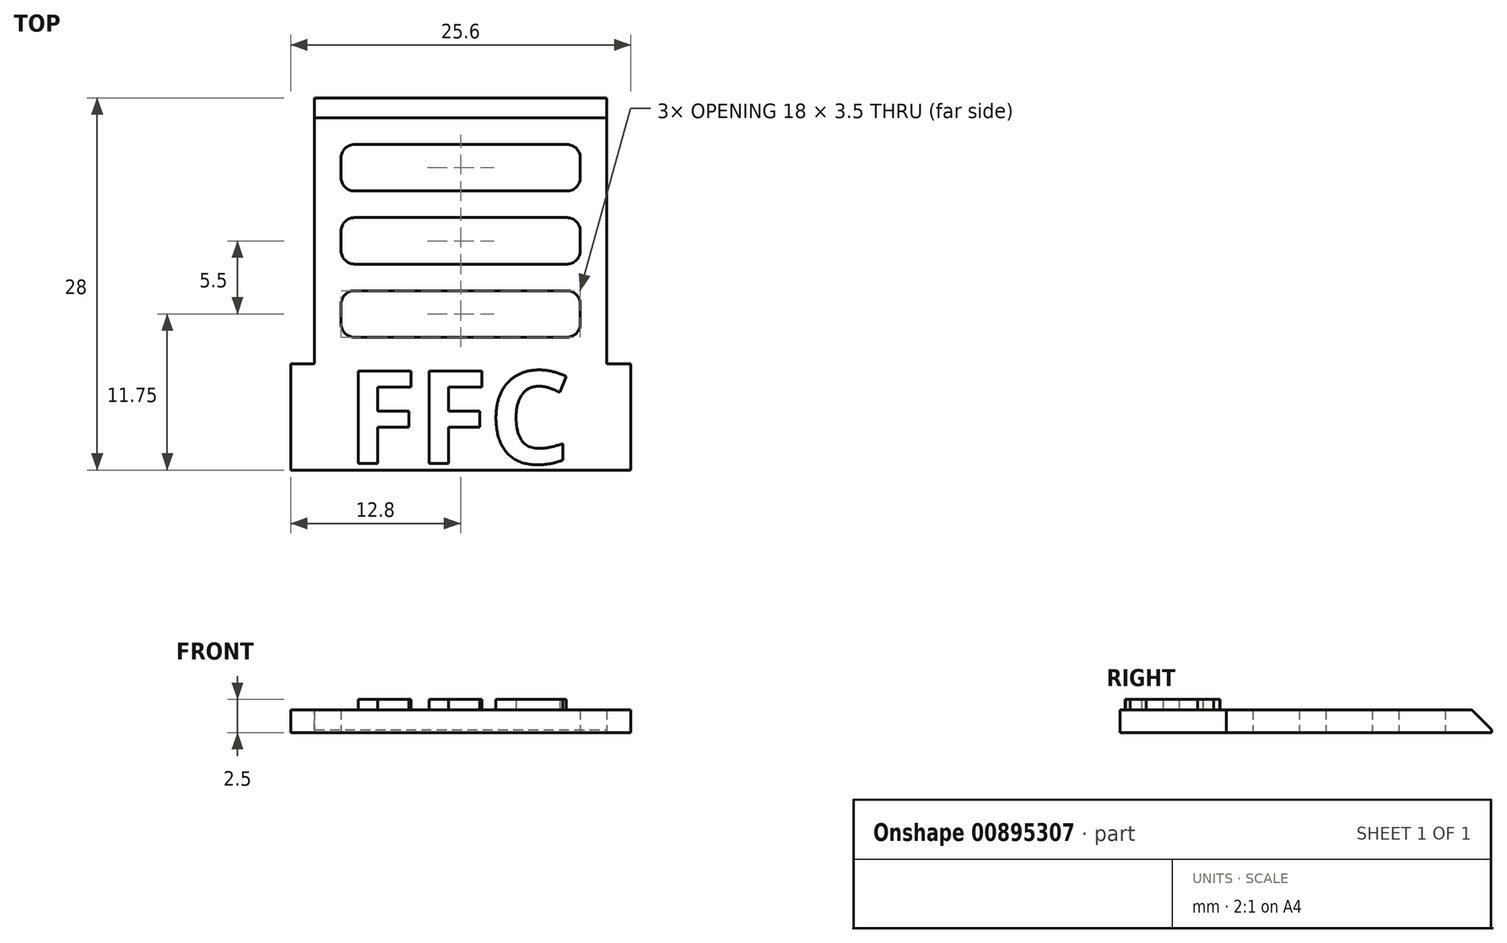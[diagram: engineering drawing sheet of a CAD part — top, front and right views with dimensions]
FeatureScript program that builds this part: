
annotation { "Feature Type Name" : "Feature", "Feature Type Description" : "" }
export const myFeature = defineFeature(function(context is Context, id is Id, definition is map)
    precondition{}
    {
        {
            var Q0;
            Q0=qCreatedBy(makeId("Top.planeOp"),FACE);
            var sketch = newSketch(context, id + "F0", { "sketchPlane" : qUnion([Q0])});
            skLineSegment(sketch, "E0.bottom", {"start": v(-11, 20) * mm, "end": v(11, 20) * mm});
            skLineSegment(sketch, "E0.top", {"start": v(-11, 0) * mm, "end": v(11, 0) * mm});
            skLineSegment(sketch, "E0.left", {"start": v(-11, 20) * mm, "end": v(-11, 0) * mm});
            skLineSegment(sketch, "E0.right", {"start": v(11, 20) * mm, "end": v(11, 0) * mm});
            skPoint(sketch, "E1", {"position": v(0, 0) * mm});
            skLineSegment(sketch, "E2.bottom", {"start": v(-12.8, 0) * mm, "end": v(12.8, 0) * mm});
            skLineSegment(sketch, "E2.top", {"start": v(-12.8, -8) * mm, "end": v(12.8, -8) * mm});
            skLineSegment(sketch, "E2.left", {"start": v(-12.8, 0) * mm, "end": v(-12.8, -8) * mm});
            skLineSegment(sketch, "E2.right", {"start": v(12.8, 0) * mm, "end": v(12.8, -8) * mm});
            skText(sketch, "E3", { "text": "FFC", "fontName": "OpenSans-Bold.ttf"});
            skLineSegment(sketch, "E4.bottom", {"start": v(-9, 16.5) * mm, "end": v(9, 16.5) * mm});
            skLineSegment(sketch, "E4.top", {"start": v(-9, 13) * mm, "end": v(9, 13) * mm});
            skLineSegment(sketch, "E4.left", {"start": v(-9, 16.5) * mm, "end": v(-9, 13) * mm});
            skLineSegment(sketch, "E4.right", {"start": v(9, 16.5) * mm, "end": v(9, 13) * mm});
            skLineSegment(sketch, "E5.bottom", {"start": v(-9, 11) * mm, "end": v(9, 11) * mm});
            skLineSegment(sketch, "E5.top", {"start": v(-9, 7.5) * mm, "end": v(9, 7.5) * mm});
            skLineSegment(sketch, "E5.left", {"start": v(-9, 11) * mm, "end": v(-9, 7.5) * mm});
            skLineSegment(sketch, "E5.right", {"start": v(9, 11) * mm, "end": v(9, 7.5) * mm});
            skLineSegment(sketch, "E6.bottom", {"start": v(-9, 5.5) * mm, "end": v(9, 5.5) * mm});
            skLineSegment(sketch, "E6.top", {"start": v(-9, 2) * mm, "end": v(9, 2) * mm});
            skLineSegment(sketch, "E6.left", {"start": v(-9, 5.5) * mm, "end": v(-9, 2) * mm});
            skLineSegment(sketch, "E6.right", {"start": v(9, 5.5) * mm, "end": v(9, 2) * mm});
            skLineSegment(sketch, "E7", {"start": v(-9, 5.5) * mm, "end": v(-9, 7.5) * mm, "construction": true});
            skLineSegment(sketch, "E8", {"start": v(-9, 11) * mm, "end": v(-9, 13) * mm, "construction": true});
            const initialGuessF0  = {"E3": [-0.00858, -0.0075, 1, 0, 0.007]};
            skSetInitialGuess(sketch, initialGuessF0);
            skSolve(sketch);
        }
        {
            var Q0;
            Q0=makeQuery(id+"F0.imprint","IMPRINT",FACE,{"disambiguationData":[TD([[makeQuery(id+"F0.imprint","IMPRINT",EDGE,{"derivedFrom":sQuery(id+"F0.wireOp",EDGE,"E2.top")}),1.0]])]});
            var Q1;
            Q1=makeQuery(id+"F0.imprint","IMPRINT",FACE,{"disambiguationData":[TD([[makeQuery(id+"F0.imprint","IMPRINT",EDGE,{"derivedFrom":sQuery(id+"F0.wireOp",EDGE,"E0.bottom")}),-1.0]])]});
            var Q2;
            Q2=makeQuery(id+"F0.imprint","IMPRINT",FACE,{"disambiguationData":[TD([[makeQuery(id+"F0.imprint","IMPRINT",EDGE,{"derivedFrom":sQuery(id+"F0.wireOp",EDGE,"E3.sketch_text.stroke-0")}),-1.0]])]});
            var Q3;
            Q3=makeQuery(id+"F0.imprint","IMPRINT",FACE,{"disambiguationData":[TD([[makeQuery(id+"F0.imprint","IMPRINT",EDGE,{"derivedFrom":sQuery(id+"F0.wireOp",EDGE,"E3.sketch_text.stroke-10")}),-1.0]])]});
            var Q4;
            Q4=makeQuery(id+"F0.imprint","IMPRINT",FACE,{"disambiguationData":[TD([[makeQuery(id+"F0.imprint","IMPRINT",EDGE,{"derivedFrom":sQuery(id+"F0.wireOp",EDGE,"E3.sketch_text.stroke-20")}),-1.0]])]});
            extrude(context, id + "F1", {"entities" : qUnion([Q0, Q1, Q2, Q3, Q4]), "depth" : 1.72 * mm, "offsetDistance" : 25 * mm});
        }
        {
            var Q0;
            Q0=makeQuery(id+"F0.imprint","IMPRINT",FACE,{"disambiguationData":[TD([[makeQuery(id+"F0.imprint","IMPRINT",EDGE,{"derivedFrom":sQuery(id+"F0.wireOp",EDGE,"E3.sketch_text.stroke-0")}),-1.0]])]});
            var Q1;
            Q1=makeQuery(id+"F0.imprint","IMPRINT",FACE,{"disambiguationData":[TD([[makeQuery(id+"F0.imprint","IMPRINT",EDGE,{"derivedFrom":sQuery(id+"F0.wireOp",EDGE,"E3.sketch_text.stroke-10")}),-1.0]])]});
            var Q2;
            Q2=makeQuery(id+"F0.imprint","IMPRINT",FACE,{"disambiguationData":[TD([[makeQuery(id+"F0.imprint","IMPRINT",EDGE,{"derivedFrom":sQuery(id+"F0.wireOp",EDGE,"E3.sketch_text.stroke-20")}),-1.0]])]});
            extrude(context, id + "F2", {"entities" : qUnion([Q0, Q1, Q2]), "operationType" : NewBodyOperationType.ADD, "depth" : 2.5 * mm, "offsetDistance" : 25 * mm});
        }
        {
            var Q0;
            Q0=makeQuery(id+"F1.opExtrude","CAP_EDGE",EDGE,{"disambiguationData":[OSD([sQuery(id+"F0.wireOp",EDGE,"E0.bottom")])],"isStart":false});
            chamfer(context, id + "F3", {"entities" : qUnion([Q0]), "width" : 1.5 * mm, "tangentPropagation" : true});
        }
        {
            var Q0;
            Q0=makeQuery(id+"F1.opExtrude","SWEPT_EDGE",EDGE,{"disambiguationData":[OSD([sQuery(id+"F0.wireOp",EDGE,"E4.bottom"),sQuery(id+"F0.wireOp",EDGE,"E4.left")])]});
            var Q1;
            Q1=makeQuery(id+"F1.opExtrude","SWEPT_EDGE",EDGE,{"disambiguationData":[OSD([sQuery(id+"F0.wireOp",EDGE,"E4.bottom"),sQuery(id+"F0.wireOp",EDGE,"E4.right")])]});
            var Q2;
            Q2=makeQuery(id+"F1.opExtrude","SWEPT_EDGE",EDGE,{"disambiguationData":[OSD([sQuery(id+"F0.wireOp",EDGE,"E5.bottom"),sQuery(id+"F0.wireOp",EDGE,"E5.right")])]});
            var Q3;
            Q3=makeQuery(id+"F1.opExtrude","SWEPT_EDGE",EDGE,{"disambiguationData":[OSD([sQuery(id+"F0.wireOp",EDGE,"E6.bottom"),sQuery(id+"F0.wireOp",EDGE,"E6.right")])]});
            var Q4;
            Q4=makeQuery(id+"F1.opExtrude","SWEPT_EDGE",EDGE,{"disambiguationData":[OSD([sQuery(id+"F0.wireOp",EDGE,"E4.top"),sQuery(id+"F0.wireOp",EDGE,"E4.right")])]});
            var Q5;
            Q5=makeQuery(id+"F1.opExtrude","SWEPT_EDGE",EDGE,{"disambiguationData":[OSD([sQuery(id+"F0.wireOp",EDGE,"E5.top"),sQuery(id+"F0.wireOp",EDGE,"E5.right")])]});
            var Q6;
            Q6=makeQuery(id+"F1.opExtrude","SWEPT_EDGE",EDGE,{"disambiguationData":[OSD([sQuery(id+"F0.wireOp",EDGE,"E6.top"),sQuery(id+"F0.wireOp",EDGE,"E6.right")])]});
            var Q7;
            Q7=makeQuery(id+"F1.opExtrude","SWEPT_EDGE",EDGE,{"disambiguationData":[OSD([sQuery(id+"F0.wireOp",EDGE,"E4.top"),sQuery(id+"F0.wireOp",EDGE,"E4.left")])]});
            var Q8;
            Q8=makeQuery(id+"F1.opExtrude","SWEPT_EDGE",EDGE,{"disambiguationData":[OSD([sQuery(id+"F0.wireOp",EDGE,"E5.top"),sQuery(id+"F0.wireOp",EDGE,"E5.left")])]});
            var Q9;
            Q9=makeQuery(id+"F1.opExtrude","SWEPT_EDGE",EDGE,{"disambiguationData":[OSD([sQuery(id+"F0.wireOp",EDGE,"E6.top"),sQuery(id+"F0.wireOp",EDGE,"E6.left")])]});
            var Q10;
            Q10=makeQuery(id+"F1.opExtrude","SWEPT_EDGE",EDGE,{"disambiguationData":[OSD([sQuery(id+"F0.wireOp",EDGE,"E6.bottom"),sQuery(id+"F0.wireOp",EDGE,"E6.left")])]});
            var Q11;
            Q11=makeQuery(id+"F1.opExtrude","SWEPT_EDGE",EDGE,{"disambiguationData":[OSD([sQuery(id+"F0.wireOp",EDGE,"E5.bottom"),sQuery(id+"F0.wireOp",EDGE,"E5.left")])]});
            fillet(context, id + "F4", {"entities" : qUnion([Q0, Q1, Q2, Q3, Q4, Q5, Q6, Q7, Q8, Q9, Q10, Q11]), "tangentPropagation" : true, "radius" : 1 * mm, "defaultsChanged" : false, "vertexSettings" : [], "allowEdgeOverflow" : false});
        }
    });
